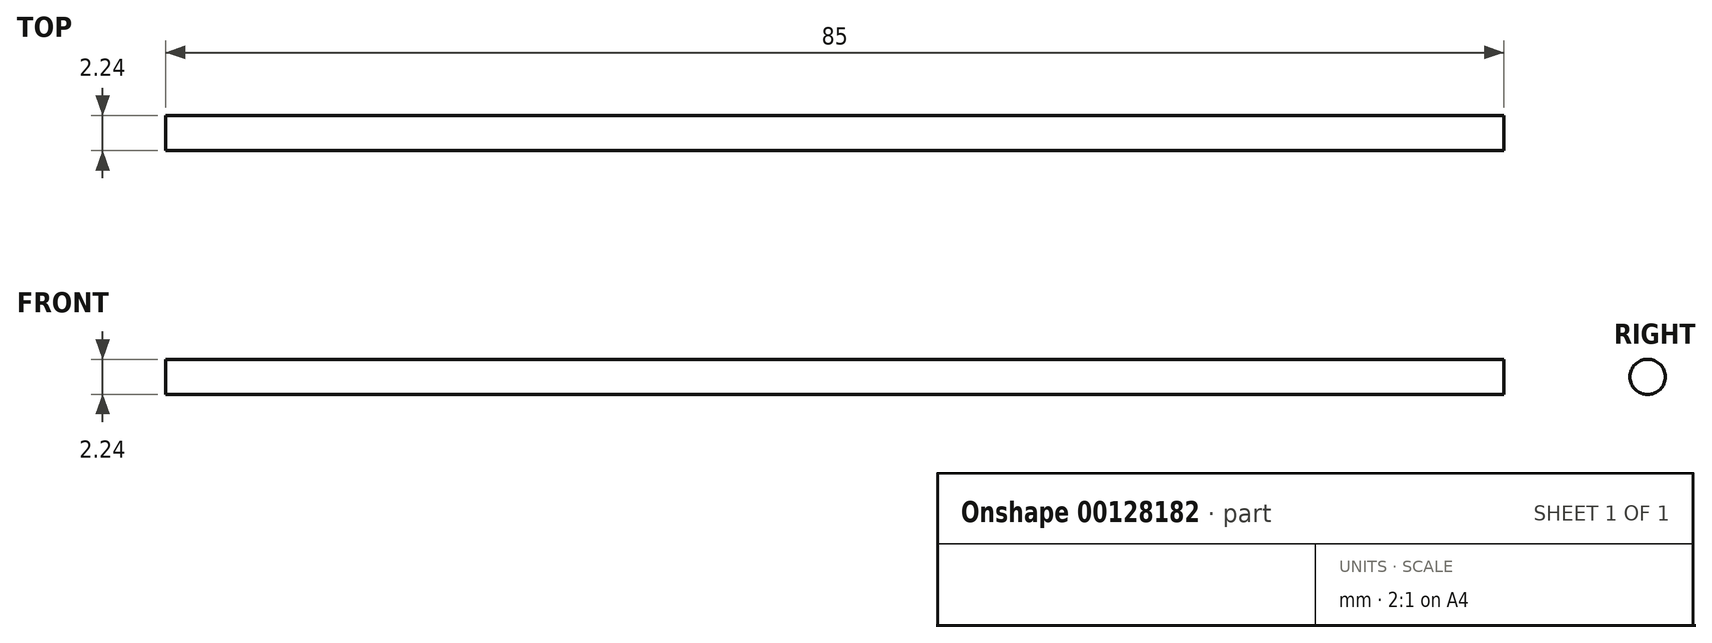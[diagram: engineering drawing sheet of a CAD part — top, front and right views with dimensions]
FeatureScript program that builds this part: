
annotation { "Feature Type Name" : "Feature", "Feature Type Description" : "" }
export const myFeature = defineFeature(function(context is Context, id is Id, definition is map)
    precondition{}
    {
        {
            var Q0;
            Q0=qCreatedBy(makeId("Front.planeOp"),FACE);
            var sketch = newSketch(context, id + "F0", { "sketchPlane" : qUnion([Q0])});
            skLineSegment(sketch, "E0", {"start": v(-42.5, 0) * mm, "end": v(42.5, 0) * mm});
            skLineSegment(sketch, "E1", {"start": v(42.5, 0) * mm, "end": v(42.5, 1.12) * mm});
            skLineSegment(sketch, "E2", {"start": v(42.5, 1.12) * mm, "end": v(-42.5, 1.12) * mm});
            skLineSegment(sketch, "E3", {"start": v(-42.5, 1.12) * mm, "end": v(-42.5, 0) * mm});
            skSolve(sketch);
        }
        {
            var Q0;
            Q0=makeQuery(id+"F0.imprint","IMPRINT",FACE,{"disambiguationData":[TD([[makeQuery(id+"F0.imprint","IMPRINT",EDGE,{"derivedFrom":sQuery(id+"F0.wireOp",EDGE,"E0")}),1.0]])]});
            var Q1;
            Q1=sQuery(id+"F0.wireOp",EDGE,"E0");
            revolve(context, id + "F1", {"entities" : qUnion([Q0]), "axis" : qUnion([Q1]), "revolveType" : RevolveType.FULL});
        }
    });
